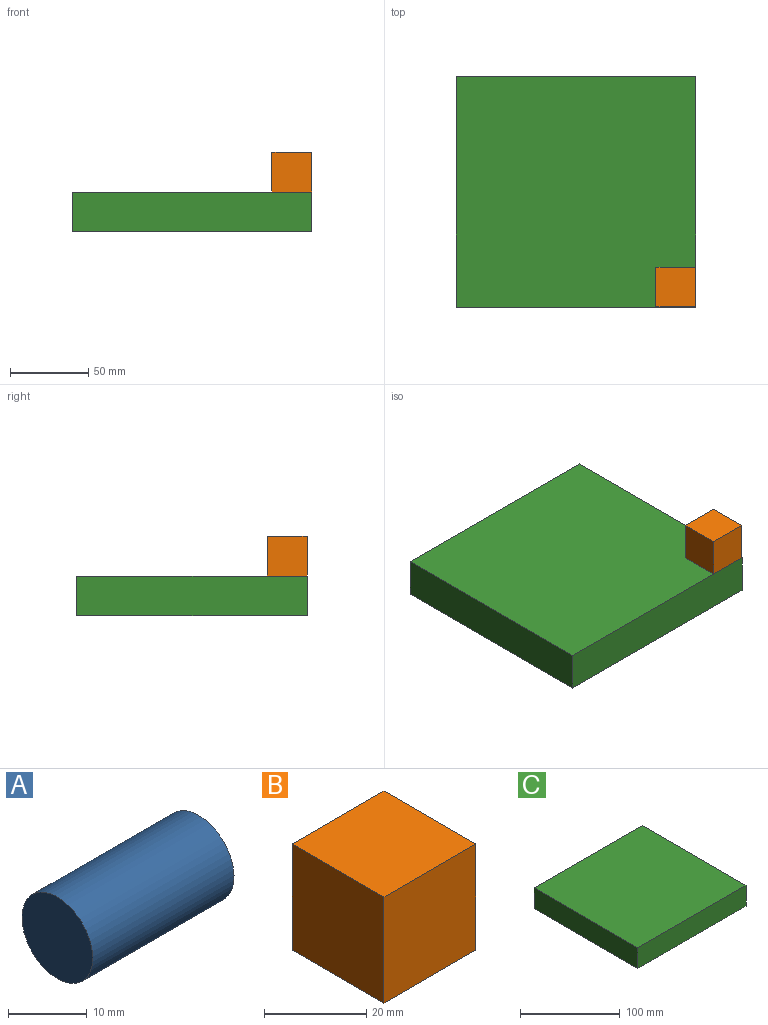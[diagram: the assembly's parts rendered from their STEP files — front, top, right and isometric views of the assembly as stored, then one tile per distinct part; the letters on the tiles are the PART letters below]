
ASSEMBLY  parts=3 mates=2
PART A: 3 faces, bbox 25.4x12.7x12.7 mm
  f0: cylinder r=6.35mm len=25.4mm, axis (-1,0,0), area 1013.4mm2, adj f1,f2
  f1: plane 12.7x12.7mm, normal (1,0,0), area 126.7mm2, adj f0
  f2: plane 12.7x12.7mm, normal (-1,0,0), area 126.7mm2, adj f0
PART B: 6 faces, bbox 25.4x25.4x25.4 mm
  f0: plane 25.4x25.4mm, normal (0,1,0), area 645.2mm2, adj f1,f3,f4,f5
  f1: plane 25.4x25.4mm, normal (-1,0,0), area 645.2mm2, adj f0,f2,f4,f5
  f2: plane 25.4x25.4mm, normal (0,-1,0), area 645.2mm2, adj f1,f3,f4,f5
  f3: plane 25.4x25.4mm, normal (1,0,0), area 645.2mm2, adj f0,f2,f4,f5
  f4: plane 25.4x25.4mm, normal (0,0,1), area 645.2mm2, adj f0,f1,f2,f3
  f5: plane 25.4x25.4mm, normal (0,0,-1), area 645.2mm2, adj f0,f1,f2,f3
PART C: 8 faces, bbox 153x147.2x25.4 mm
  f0: plane 153x25.4mm, normal (0,1,0), area 3886.2mm2, adj f1,f3,f4,f5
  f1: plane 147.16x25.4mm, normal (-1,0,0), area 3737.7mm2, adj f0,f2,f4,f5
  f2: plane 153x25.4mm, normal (0,-1,0), area 3886.2mm2, adj f1,f3,f4,f5
  f3: plane 147.16x25.4mm, normal (1,0,0), area 3572.1mm2, adj f0,f2,f4,f5,f6
  f4: plane 153x147.16mm, normal (0,0,1), area 22514.9mm2, adj f0,f1,f2,f3
  f5: plane 153x147.16mm, normal (0,0,-1), area 22514.9mm2, adj f0,f1,f2,f3
  f6: cylinder r=7.26mm len=25.4mm, axis (1,0,0), area 1158.9mm2, adj f3,f7
  f7: plane 14.52x14.52mm, normal (1,0,0), area 165.7mm2, adj f6
PLACE A t=(-64.7,20.09,79.75)mm
PLACE B t=(-51.8,-20.41,93.05)mm
PLACE C t=(-117.26,27.32,67.65)mm
MATE fastened C.f3 <-> B.f3  axis (1,0,0) through (-39.3,-37.19,93.05)mm
MATE fastened A.f0 <-> C.f6  axis (-1,0,0) through (-64.7,20.09,79.75)mm
